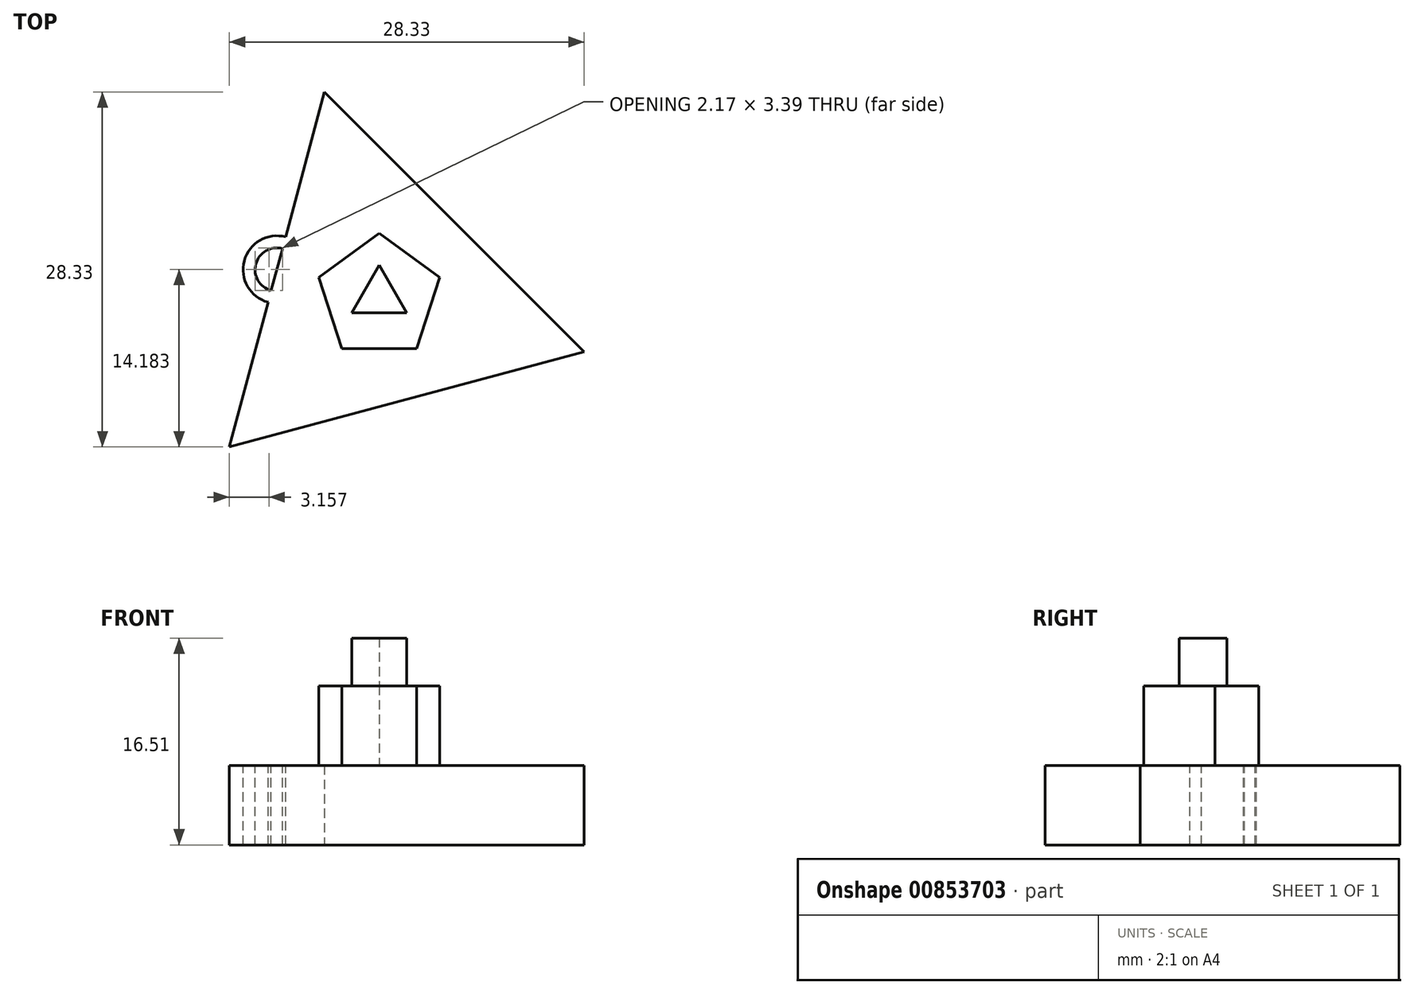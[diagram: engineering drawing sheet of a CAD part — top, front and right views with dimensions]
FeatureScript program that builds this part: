
annotation { "Feature Type Name" : "Feature", "Feature Type Description" : "" }
export const myFeature = defineFeature(function(context is Context, id is Id, definition is map)
    precondition{}
    {
        {
            var Q0;
            Q0=qCreatedBy(makeId("Top.planeOp"),FACE);
            var sketch = newSketch(context, id + "F0", { "sketchPlane" : qUnion([Q0])});
            skCircle(sketch, "E0.cCircle", {"center": v(0, 0) * mm, "radius": 8.47 * mm, "construction": true});
            skLineSegment(sketch, "E0.0", {"start": v(-4.38, 16.36) * mm, "end": v(16.36, -4.38) * mm});
            skLineSegment(sketch, "E0.1", {"start": v(16.36, -4.38) * mm, "end": v(-11.97, -11.97) * mm});
            skLineSegment(sketch, "E0.2", {"start": v(-11.97, -11.97) * mm, "end": v(-4.38, 16.36) * mm});
            skPoint(sketch, "E0.0.midPoint", {"position": v(5.99, 5.99) * mm});
            skSolve(sketch);
        }
        {
            var Q0;
            Q0=makeQuery(id+"F0.imprint","IMPRINT",FACE,{"disambiguationData":[TD([[makeQuery(id+"F0.imprint","IMPRINT",EDGE,{"derivedFrom":sQuery(id+"F0.wireOp",EDGE,"E0.0")}),-1.0]])]});
            extrude(context, id + "F1", {"entities" : qUnion([Q0]), "depth" : 6.35 * mm, "offsetDistance" : 25.4 * mm});
        }
        {
            var Q0;
            Q0=makeQuery(id+"F1.opExtrude","CAP_FACE",FACE,{"disambiguationData":[OSD([sQuery(id+"F0.wireOp",EDGE,"E0.0"),sQuery(id+"F0.wireOp",EDGE,"E0.1"),sQuery(id+"F0.wireOp",EDGE,"E0.2")])],"isStart":false});
            var sketch = newSketch(context, id + "F2", { "sketchPlane" : qUnion([Q0])});
            skCircle(sketch, "E1.cCircle", {"center": v(0, 0) * mm, "radius": 4.1 * mm, "construction": true});
            skLineSegment(sketch, "E1.0", {"start": v(2.99, -4.1) * mm, "end": v(-2.99, -4.1) * mm});
            skLineSegment(sketch, "E1.1", {"start": v(-2.99, -4.1) * mm, "end": v(-4.83, 1.57) * mm});
            skLineSegment(sketch, "E1.2", {"start": v(-4.83, 1.57) * mm, "end": v(0, 5.08) * mm});
            skLineSegment(sketch, "E1.3", {"start": v(0, 5.08) * mm, "end": v(4.83, 1.57) * mm});
            skLineSegment(sketch, "E1.4", {"start": v(4.83, 1.57) * mm, "end": v(2.99, -4.1) * mm});
            skPoint(sketch, "E1.0.midPoint", {"position": v(0, -4.1) * mm});
            skSolve(sketch);
        }
        {
            var Q0;
            Q0 = qSketchRegion(id + "F2", true);
            extrude(context, id + "F3", {"entities" : qUnion([Q0]), "operationType" : NewBodyOperationType.ADD, "depth" : 6.35 * mm, "offsetDistance" : 25.4 * mm});
        }
        {
            var Q0;
            Q0=makeQuery(id+"F3.opExtrude","CAP_FACE",FACE,{"disambiguationData":[OSD([sQuery(id+"F2.wireOp",EDGE,"E1.0"),sQuery(id+"F2.wireOp",EDGE,"E1.1"),sQuery(id+"F2.wireOp",EDGE,"E1.2"),sQuery(id+"F2.wireOp",EDGE,"E1.3"),sQuery(id+"F2.wireOp",EDGE,"E1.4")])],"isStart":false});
            var sketch = newSketch(context, id + "F4", { "sketchPlane" : qUnion([Q0])});
            skCircle(sketch, "E2.cCircle", {"center": v(0, 0) * mm, "radius": 1.27 * mm, "construction": true});
            skPoint(sketch, "E2.cCircle.perimeterSnap0", {"position": v(0, -4.1) * mm});
            skLineSegment(sketch, "E2.0", {"start": v(2.2, -1.27) * mm, "end": v(-2.2, -1.27) * mm});
            skLineSegment(sketch, "E2.1", {"start": v(-2.2, -1.27) * mm, "end": v(0, 2.54) * mm});
            skLineSegment(sketch, "E2.2", {"start": v(0, 2.54) * mm, "end": v(2.2, -1.27) * mm});
            skPoint(sketch, "E2.0.midPoint", {"position": v(0, -1.27) * mm});
            skPoint(sketch, "E2.0.midPoint.positionSnap0", {"position": v(0, -4.1) * mm});
            skSolve(sketch);
        }
        {
            var Q0;
            Q0=makeQuery(id+"F4.imprint","IMPRINT",FACE,{"disambiguationData":[TD([[makeQuery(id+"F4.imprint","IMPRINT",EDGE,{"derivedFrom":sQuery(id+"F4.wireOp",EDGE,"E2.0")}),-1.0]])]});
            extrude(context, id + "F5", {"entities" : qUnion([Q0]), "operationType" : NewBodyOperationType.ADD, "depth" : 3.8 * mm, "offsetDistance" : 25.4 * mm});
        }
        {
            var Q0;
            Q0=makeQuery(id+"F1.opExtrude","CAP_FACE",FACE,{"disambiguationData":[OSD([sQuery(id+"F0.wireOp",EDGE,"E0.0"),sQuery(id+"F0.wireOp",EDGE,"E0.1"),sQuery(id+"F0.wireOp",EDGE,"E0.2")])],"isStart":false});
            var sketch = newSketch(context, id + "F6", { "sketchPlane" : qUnion([Q0])});
            skCircle(sketch, "E3", {"center": v(-8.18, 2.2) * mm, "radius": 1.73 * mm});
            skCircle(sketch, "E4", {"center": v(-8.18, 2.2) * mm, "radius": 2.7 * mm});
            skSolve(sketch);
        }
        {
            var Q0;
            Q0 = qSketchRegion(id + "F6", true);
            extrude(context, id + "F7", {"entities" : qUnion([Q0]), "operationType" : NewBodyOperationType.ADD, "oppositeDirection" : true, "depth" : 6.35 * mm, "offsetDistance" : 25.4 * mm});
        }
    });
